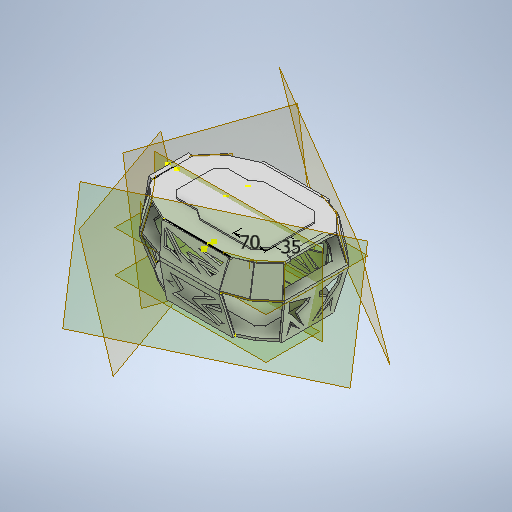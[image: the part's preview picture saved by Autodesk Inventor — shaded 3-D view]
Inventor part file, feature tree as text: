
AUTODESK INVENTOR PART (.ipt)
format: ipt  version: 2025.2 (Build 292293000, 293)  size: 6,136,832 bytes
history: native  units: mm
features: sketch x50, extrude x37, other x23, plane x17, loft x11, mirror x2, chamfer x2
ambient origin geometry x8: Origin, YZ Plane, XZ Plane, XY Plane, X Axis, Y Axis, Z Axis, Center Point
bodies: Body1 (feature_tree)
feature tree (142):
  extrude  "Extrusion2"  Depth=45.0mm
  extrude  "Extrusion3"  Depth=40.0mm
  plane  "Work Plane3"
  extrude  "Extrusion4"  Depth=145.0mm
  extrude  "Extrusion5"  Depth=55.0mm
  plane  "Work Plane4"
  extrude  "Extrusion6"  Depth=40.0mm
  sketch  "Sketch8"  dims[d17=165.0deg d18=15.0mm]
  sketch  "Sketch9"  dims[d20=10.0mm d21=40.0mm]
  sketch  "Sketch10"  dims[d22=5.0mm d23=5.0mm]
  loft  "Loft1"
  loft  "Loft2"
  extrude  "Extrusion7"  Depth=5.0mm
  extrude  "Extrusion8"  TaperAngle=90.0deg  [1 undecoded]
  extrude  "Extrusion9"  Depth=30.0mm
  sketch  "Sketch14"  dims[d30=45.0mm d31=20.0mm]
  sketch  "Sketch15"  dims[d32=45.0deg d39=5.0mm d40=0.0mm]
  sketch  "Sketch16"  dims[d41=3.0mm d42=3.0mm d43=0.0mm d44=0.0mm d45=150.0mm]
  loft  "Loft3"
  loft  "Loft4"
  loft  "Loft5"
  extrude  "Extrusion10"  Depth=150.0mm
  extrude  "Extrusion11"  Depth=10.0mm
  extrude  "Extrusion12"  Depth=10.0mm
  extrude  "Extrusion13"  Depth=10.0mm
  extrude  "Extrusion14"  Depth=10.0mm
  loft  "Loft7"
  loft  "Loft8"
  sketch  "Sketch22"  dims[d57=10.0mm d58=10.0mm]
  plane  "Work Plane5"
  extrude  "Extrusion15"  Depth=3.0mm TaperAngle=0.0deg
  plane  "Work Plane6"
  extrude  "Extrusion16"  Depth=10.0mm
  extrude  "Extrusion17"  Depth=50.0mm
  plane  "Work Plane7"
  extrude  "Extrusion18"  Depth=50.0mm
  sketch  "Sketch28"  dims[d71=27.925268mm d72=10.0mm]
  extrude  "Extrusion19"  Depth=10.0mm
  extrude  "Extrusion20"  Depth=60.0mm
  extrude  "Extrusion21"  Depth=5.0mm TaperAngle=0.0deg
  extrude  "Extrusion22"  TaperAngle=0.0deg  [1 undecoded]
  extrude  "Extrusion23"  TaperAngle=0.0deg  [1 undecoded]
  extrude  "Extrusion24"  Depth=4.0mm TaperAngle=0.0deg
  extrude  "Extrusion25"  TaperAngle=0.0deg  [1 undecoded]
  extrude  "Extrusion26"  TaperAngle=0.0deg  [1 undecoded]
  extrude  "Extrusion27"  TaperAngle=0.0deg  [1 undecoded]
  plane  "Work Plane8"
  mirror  "Mirror1"
  loft  "Loft9"
  loft  "Loft10"
  loft  "Loft11"
  loft  "Loft12"
  plane  "Work Plane14"
  plane  "Work Plane15"
  extrude  "Extrusion28"  TaperAngle=0.0deg  [1 undecoded]
  extrude  "Extrusion29"  Depth=4.0mm TaperAngle=0.0deg
  plane  "Work Plane16"
  extrude  "Extrusion30"  Depth=4.0mm
  mirror  "Mirror2"
  extrude  "Extrusion31"  Depth=70.0mm
  sketch  "Sketch42"  dims[d126=4.0mm d127=0.0mm d128=4.0mm d129=0.0mm]
  extrude  "Extrusion32"  Depth=10.0mm
  extrude  "Extrusion33"  Depth=70.0mm
  extrude  "Extrusion34"  Depth=35.0mm
  extrude  "Extrusion35"  Depth=23.0mm TaperAngle=0.0deg
  chamfer  "Chamfer1"  Distance=17.5mm
  extrude  "Extrusion36"  Depth=30.0mm
  chamfer  "Chamfer2"  Distance=5.0mm
  sketch  "Sketch48"  dims[d142=90.0deg d143=23.0mm d144=0.0mm]
  extrude  "Extrusion37"  Depth=20.0mm
  extrude  "Extrusion38"  TaperAngle=90.0deg  [1 undecoded]
  sketch  "Sketch51"  dims[d149=25.0mm d150=30.0mm]
  sketch  "Sketch52"  dims[d151=15.0deg]
  sketch  "Sketch53"  dims[d152=90.0deg d153=5.0mm d154=20.0mm d155=90.0deg d156=4.363323mm d157=17.5mm d158=0.0mm d159=25.0mm d160=165.0deg d161=40.0mm d162=150.0deg d163=50.0mm d164=1.745329mm d165=40.0mm d166=5.0mm d167=40.0mm d168=30.543262mm d169=17.5mm d170=0.0mm d171=10.0mm d172=100.0mm d173=150.0deg d174=40.0mm d175=19.198622mm d176=100.0mm d177=70.0mm d178=30.0deg d179=100.0mm d180=10.0mm d181=10.0mm d182=10.0mm d183=4.363323mm d184=40.0mm d185=40.0mm d186=6.981317mm d187=20.0mm d188=24.43461mm d189=16.0mm d190=10.0mm d191=0.0mm d192=80.0mm d193=24.43461mm d194=120.0mm d195=30.0deg d196=40.0mm d197=30.0deg d198=50.0mm d199=10.0mm d200=50.0mm d201=55.0mm d202=1.745329mm d203=30.0mm d204=27.925268mm d205=40.0mm d206=5.0mm d207=30.0mm d208=30.0mm d209=17.453293mm d210=60.0mm d211=30.0mm d212=50.0mm d213=0.0mm d214=10.0mm d215=10.0mm d216=10.0mm d217=10.0mm d218=90.0deg d219=10.0mm d220=20.0mm d221=10.0mm d222=17.453293mm d223=25.0mm d224=22.68928mm d225=70.0mm d226=10.0mm d227=40.0mm d228=22.68928mm d229=20.0mm d230=75.0deg d231=50.0mm d232=0.0mm d233=5.0mm d234=0.0mm d235=5.0mm d236=0.0mm d238=0.0mm d239=90.0deg d240=0.0mm d241=90.0deg d242=0.0mm d243=90.0deg d244=0.0mm d245=90.0deg d246=0.0mm d247=90.0deg d248=0.0mm d249=90.0deg d250=0.0mm d251=90.0deg d252=0.0mm d253=90.0deg d254=3.0mm d255=0.0mm d256=3.0mm d257=0.0mm d258=3.0mm d259=0.0mm d260=30.0mm d261=50.0mm d262=90.0mm d263=30.0mm d264=5.0mm d265=0.0mm d266=20.0mm d267=100.0mm d268=20.0mm d269=100.0mm d270=30.0mm d271=40.0mm d272=30.0mm d273=5.0mm d274=5.0mm d275=0.0mm d276=0.0mm d277=10.0mm d278=10.0mm d279=30.0mm d280=0.0mm d281=20.0mm d282=20.0mm d283=20.0mm d284=90.0deg d285=10.0mm d286=0.0mm d287=20.0mm d288=100.0mm d289=0.0mm d290=10.0mm d291=10.0mm d292=10.0mm d293=0.0mm d294=6.0mm d295=2.0mm d296=45.0deg d297=20.0mm d298=13.0mm d299=20.0mm d300=13.0mm d301=20.0mm d302=13.0mm d303=20.0mm d304=13.0mm d305=20.0mm d306=0.0mm d307=20.0mm d308=2.0mm d309=45.0deg d310=140.0mm d311=10.0mm d312=23.0mm d313=0.0mm d314=50.0mm d315=0.0mm]
  sketch  "Sketch1"  dims[d6=115.0mm d8=45.0mm]
  other  "Image1"
  sketch  "Sketch3"  dims[d9=45.0deg d10=40.0mm]
  sketch  "Sketch4"  dims[d11=27.925268mm d12=145.0mm]
  sketch  "Sketch5"  dims[d13=27.052603mm d14=55.0mm]
  sketch  "Sketch6"  dims[d15=27.052603mm d16=40.0mm]
  other  "Edges1"
  other  "Edges2"
  other  "Edges3"
  other  "Edges4"
  sketch  "Sketch11"  dims[d24=40.0mm d25=90.0deg]
  sketch  "Sketch12"  dims[d26=30.0mm d27=110.0mm]
  sketch  "Sketch13"  dims[d28=25.0mm d29=25.307274mm]
  other  "Edges5"
  other  "Edges6"
  other  "Edges7"
  other  "Edges8"
  other  "Edges9"
  other  "Edges10"
  sketch  "Sketch17"  dims[d46=10.0mm d48=10.0mm]
  sketch  "Sketch18"  dims[d49=10.0mm d50=22.68928mm]
  sketch  "Sketch19"  dims[d51=10.0mm d52=10.0mm]
  sketch  "Sketch20"  dims[d53=10.0mm d54=10.0mm]
  sketch  "Sketch21"  dims[d55=10.0mm d56=10.0mm]
  other  "Edges13"
  other  "Edges14"
  other  "Edges15"
  other  "Edges16"
  sketch  "Sketch23"  dims[d59=5.0mm d60=0.0mm d61=3.0mm d62=3.0mm d63=0.0mm d64=0.0mm]
  sketch  "Sketch24"  dims[d65=-90.0mm d66=10.0mm]
  sketch  "Sketch25"  dims[d67=70.0mm d68=50.0mm]
  sketch  "Sketch26"  dims[d69=22.68928mm d70=50.0mm]
  sketch  "Sketch29"  dims[d73=50.0mm d74=60.0mm]
  sketch  "Sketch30"  dims[d75=70.0mm d76=5.0mm d77=0.0mm]
  sketch  "Sketch31"  dims[d78=0.0mm d79=90.0deg d80=0.0mm d81=90.0deg]
  sketch  "Sketch32"  dims[d82=0.0mm d83=90.0deg d84=0.0mm d85=90.0deg]
  sketch  "Sketch33"  dims[d86=4.0mm d87=0.0mm d88=4.0mm d89=0.0mm]
  sketch  "Sketch34"  dims[d90=4.0mm d91=0.0mm d92=0.0mm d93=90.0deg]
  sketch  "Sketch35"  dims[d94=0.0mm d95=90.0deg d96=0.0mm d97=90.0deg]
  sketch  "Sketch36"  dims[d98=0.0mm d99=90.0deg d100=0.0mm d101=90.0deg]
  sketch  "Sketch37"  dims[d102=0.0mm d103=90.0deg d104=4.0mm d105=0.0mm]
  plane  "Work Plane9"
  plane  "Work Plane10"
  plane  "Work Plane11"
  plane  "Work Plane12"
  plane  "Work Plane13"
  other  "Edges17"
  other  "Edges18"
  other  "Edges19"
  other  "Edges20"
  other  "Edges21"
  other  "Edges22"
  other  "Edges23"
  other  "Edges24"
  sketch  "Sketch38"  dims[d106=4.0mm d107=0.0mm d108=4.0mm d109=0.0mm]
  sketch  "Sketch39"  dims[d110=4.0mm d111=0.0mm d112=4.0mm d113=0.0mm]
  sketch  "Sketch40"  dims[d118=0.0mm d119=90.0deg d120=0.0mm d121=90.0deg]
  plane  "Work Plane17"
  plane  "Work Plane18"
  plane  "Work Plane19"
  sketch  "Sketch41"  dims[d122=0.0mm d123=90.0deg d124=0.0mm d125=90.0deg]
  sketch  "Sketch43"  dims[d130=4.0mm d131=0.0mm d132=92.689mm]
  sketch  "Sketch44"  dims[d133=4.0mm d134=0.0mm d135=70.0mm]
  sketch  "Sketch45"  dims[d136=35.0mm d137=10.0mm]
  sketch  "Sketch46"  dims[d138=50.0mm d139=70.0mm]
  sketch  "Sketch47"  dims[d140=50.0mm d141=35.0mm]
  sketch  "Sketch49"  dims[d145=70.0mm]
  sketch  "Sketch50"  dims[d146=3.0mm d147=17.5mm d148=0.0mm]
note: 8 required parameter values undecoded (feature->parameter linkage not recoverable at this tier; creation-order binding heuristic only, values carry confidence <= 0.55)
